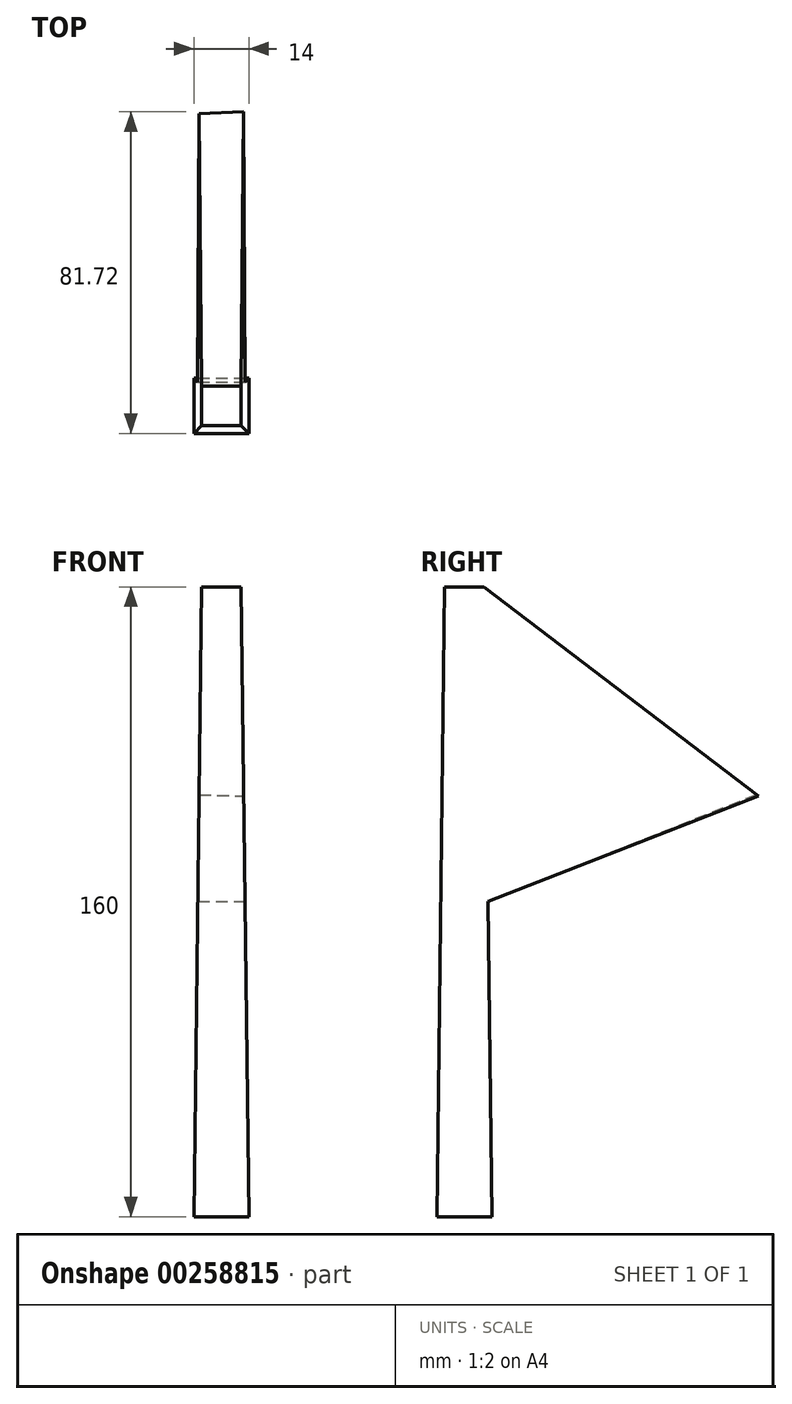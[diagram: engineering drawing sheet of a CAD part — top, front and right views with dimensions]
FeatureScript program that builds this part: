
annotation { "Feature Type Name" : "Feature", "Feature Type Description" : "" }
export const myFeature = defineFeature(function(context is Context, id is Id, definition is map)
    precondition{}
    {
        {
            var Q0;
            Q0=qCreatedBy(makeId("Top.planeOp"),FACE);
            cPlane(context, id + "F0", {"entities" : qUnion([Q0]), "cplaneType" : CPlaneType.OFFSET, "offset" : 80 * mm, "oppositeDirection" : true, "width" : 150 * mm, "height" : 150 * mm});
        }
        {
            var Q0;
            Q0=qCreatedBy(makeId("Top.planeOp"),FACE);
            cPlane(context, id + "F1", {"entities" : qUnion([Q0]), "cplaneType" : CPlaneType.OFFSET, "offset" : 80 * mm, "width" : 150 * mm, "height" : 150 * mm});
        }
        {
            var Q0;
            Q0=qCreatedBy(id+"F0.planeOp",FACE);
            var sketch = newSketch(context, id + "F2", { "sketchPlane" : qUnion([Q0])});
            skLineSegment(sketch, "E0.bottom", {"start": v(-7, 7) * mm, "end": v(7, 7) * mm});
            skLineSegment(sketch, "E0.top", {"start": v(-7, -7) * mm, "end": v(7, -7) * mm});
            skLineSegment(sketch, "E0.left", {"start": v(-7, 7) * mm, "end": v(-7, -7) * mm});
            skLineSegment(sketch, "E0.right", {"start": v(7, 7) * mm, "end": v(7, -7) * mm});
            skSolve(sketch);
        }
        {
            var Q0;
            Q0=qCreatedBy(id+"F1.planeOp",FACE);
            var sketch = newSketch(context, id + "F3", { "sketchPlane" : qUnion([Q0])});
            skLineSegment(sketch, "E1.bottom", {"start": v(-5, 5) * mm, "end": v(5, 5) * mm});
            skLineSegment(sketch, "E1.top", {"start": v(-5, -5) * mm, "end": v(5, -5) * mm});
            skLineSegment(sketch, "E1.left", {"start": v(-5, 5) * mm, "end": v(-5, -5) * mm});
            skLineSegment(sketch, "E1.right", {"start": v(5, 5) * mm, "end": v(5, -5) * mm});
            skSolve(sketch);
        }
        {
            var Q0;
            Q0=makeQuery(id+"F3.imprint","IMPRINT",FACE,{"disambiguationData":[TD([[makeQuery(id+"F3.imprint","IMPRINT",EDGE,{"derivedFrom":sQuery(id+"F3.wireOp",EDGE,"E1.bottom")}),-1.0]])]});
            var Q1;
            Q1=makeQuery(id+"F2.imprint","IMPRINT",FACE,{"disambiguationData":[TD([[makeQuery(id+"F2.imprint","IMPRINT",EDGE,{"derivedFrom":sQuery(id+"F2.wireOp",EDGE,"E0.bottom")}),-1.0]])]});
            loft(context, id + "F4", {"sheetProfilesArray" : [{ "sheetProfileEntities" : qUnion([Q0]) }, { "sheetProfileEntities" : qUnion([Q1]) }]});
        }
        {
            var Q0;
            Q0=makeQuery(id+"F4.opLoft","SWEPT_FACE",FACE,{"disambiguationData":[OSD([sQuery(id+"F2.wireOp",EDGE,"E0.bottom"),sQuery(id+"F2.wireOp",EDGE,"E0.top"),sQuery(id+"F2.wireOp",EDGE,"E0.right"),sQuery(id+"F3.wireOp",EDGE,"E1.bottom"),sQuery(id+"F3.wireOp",EDGE,"E1.top"),sQuery(id+"F3.wireOp",EDGE,"E1.right")])]});
            var sketch = newSketch(context, id + "F5", { "sketchPlane" : qUnion([Q0])});
            skLineSegment(sketch, "E2", {"start": v(5, 79.93) * mm, "end": v(74.72, 26.77) * mm});
            skLineSegment(sketch, "E3", {"start": v(74.72, 26.77) * mm, "end": v(6, 0) * mm});
            skSolve(sketch);
        }
        {
            var Q0;
            Q0=makeQuery(id+"F4.opLoft","SWEPT_FACE",FACE,{"disambiguationData":[OSD([sQuery(id+"F2.wireOp",EDGE,"E0.bottom"),sQuery(id+"F2.wireOp",EDGE,"E0.top"),sQuery(id+"F2.wireOp",EDGE,"E0.left"),sQuery(id+"F3.wireOp",EDGE,"E1.bottom"),sQuery(id+"F3.wireOp",EDGE,"E1.top"),sQuery(id+"F3.wireOp",EDGE,"E1.left")])]});
            var sketch = newSketch(context, id + "F6", { "sketchPlane" : qUnion([Q0])});
            skLineSegment(sketch, "E4", {"start": v(-5, 79.93) * mm, "end": v(-74.25, 27.1) * mm});
            skLineSegment(sketch, "E5", {"start": v(-74.25, 27.1) * mm, "end": v(-6, 0) * mm});
            skSolve(sketch);
        }
        {
            var Q1;
            {var subQ0=sQuery(id+"F6.wireOp",EDGE,"E4");Q1=makeQuery(id+"F6.imprint","IMPRINT",FACE,{"disambiguationData":[TD([[makeQuery(id+"F6.imprint","IMPRINT",EDGE,{"derivedFrom":subQ0}),1.0]])]});}
            var Q2;
            {var subQ0=sQuery(id+"F5.wireOp",EDGE,"E2");Q2=makeQuery(id+"F5.imprint","IMPRINT",FACE,{"disambiguationData":[TD([[makeQuery(id+"F5.imprint","IMPRINT",EDGE,{"derivedFrom":subQ0}),-1.0]])]});}
            loft(context, id + "F7", {"operationType" : NewBodyOperationType.ADD, "sheetProfilesArray" : [{ "sheetProfileEntities" : qUnion([Q1]) }, { "sheetProfileEntities" : qUnion([Q2]) }]});
        }
    });
